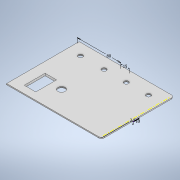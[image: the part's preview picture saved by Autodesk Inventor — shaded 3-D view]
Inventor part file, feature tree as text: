
AUTODESK INVENTOR PART (.ipt)
format: ipt  version: 2021 (Build 250183000, 183)  size: 274,432 bytes
history: native  units: mm
features: sketch x12, extrude x8, hole x4, chamfer x3, projected_geometry x3, fillet x1
ambient origin geometry x8: Origin, YZ Plane, XZ Plane, XY Plane, X Axis, Y Axis, Z Axis, Center Point
bodies: Volumenkörper1 (feature_tree)
feature tree (31):
  extrude  "Extrusion1"  Depth=120.0mm
  chamfer  "Fase1"  Distance=3.0mm
  extrude  "Extrusion2"  Depth=10.0mm
  extrude  "Extrusion3"  Depth=2.0mm
  hole  "Bohrung1"  [1 undecoded]
  hole  "Bohrung2"  [1 undecoded]
  hole  "Bohrung3"  [1 undecoded]
  hole  "Bohrung4"  [1 undecoded]
  extrude  "Extrusion4"  Depth=7.0mm
  extrude  "Extrusion5"  Depth=7.0mm
  fillet  "Rundung1"  Radius=7.0mm
  sketch  "Skizze10"  dims[d10=137.0mm]
  extrude  "Extrusion6"  Depth=3.5mm
  extrude  "Extrusion7"  Depth=3.5mm
  chamfer  "Fase2"  Distance=3.5mm
  chamfer  "Fase3"  Distance=7.0mm
  extrude  "Extrusion8"  Depth=3.5mm
  sketch  "Skizze12"  dims[d12=34.0mm d13=3.0mm d14=10.0mm d15=13.0mm d16=28.5mm d17=48.5mm d18=2.0mm d19=0.0mm d20=2.0mm d21=2.0mm d22=45.0deg d23=7.0mm d24=7.0mm d25=7.0mm d26=3.5mm d28=3.5mm d29=3.5mm d30=7.0mm d31=3.5mm d32=87.0mm d33=87.0mm d34=4.5mm d35=0.0mm d36=2.5mm d37=0.0mm d38=3.0mm d39=6.0mm d40=4.0mm d41=2.0mm d42=90.0deg d43=5.0mm d44=0.0mm d45=3.0mm d46=6.0mm d47=4.0mm d48=2.0mm d49=90.0deg d50=7.0mm d51=0.0mm d52=3.0mm d53=6.0mm d54=4.0mm d55=2.0mm d56=90.0deg d57=7.0mm d58=0.0mm d59=3.0mm d60=6.0mm d61=4.0mm d62=2.0mm d63=90.0deg d64=5.0mm d65=0.0mm d66=25.0mm d67=25.0mm d68=2.0mm d69=0.0mm d70=2.7mm d71=2.7mm d72=0.0mm d73=2.7mm d74=2.0mm d75=2.0mm d76=2.0mm d77=2.0mm d78=2.0mm d79=0.0mm d80=4.75mm d81=132.239418mm d83=1.0mm d84=2.0mm d85=0.0mm d86=0.4mm d87=0.0mm d88=0.25mm d89=2.0mm d90=45.0deg d91=10.0mm d92=2.5mm d93=2.0mm d94=2.0mm d95=30.0deg d96=3.2mm d97=0.0mm d98=15.0mm d99=80.0mm]
  sketch  "Skizze1"  dims[d0=150.0mm d1=120.0mm]
  sketch  "Skizze2"  dims[d2=8.0mm]
  sketch  "Skizze3"  dims[d3=98.5mm]
  projected_geometry  "Projizierte Kontur1"
  projected_geometry  "Projizierte Kontur2"
  sketch  "Skizze4"  dims[d4=13.0mm]
  sketch  "Skizze5"  dims[d5=8.0mm]
  sketch  "Skizze6"  dims[d6=8.0mm]
  sketch  "Skizze7"  dims[d7=8.0mm]
  projected_geometry  "Projizierte Kontur3"
  sketch  "Skizze8"  dims[d8=56.0mm]
  sketch  "Skizze9"  dims[d9=96.5mm]
  sketch  "Skizze11"  dims[d11=17.0mm]
note: 4 required parameter values undecoded (feature->parameter linkage not recoverable at this tier; creation-order binding heuristic only, values carry confidence <= 0.55)
